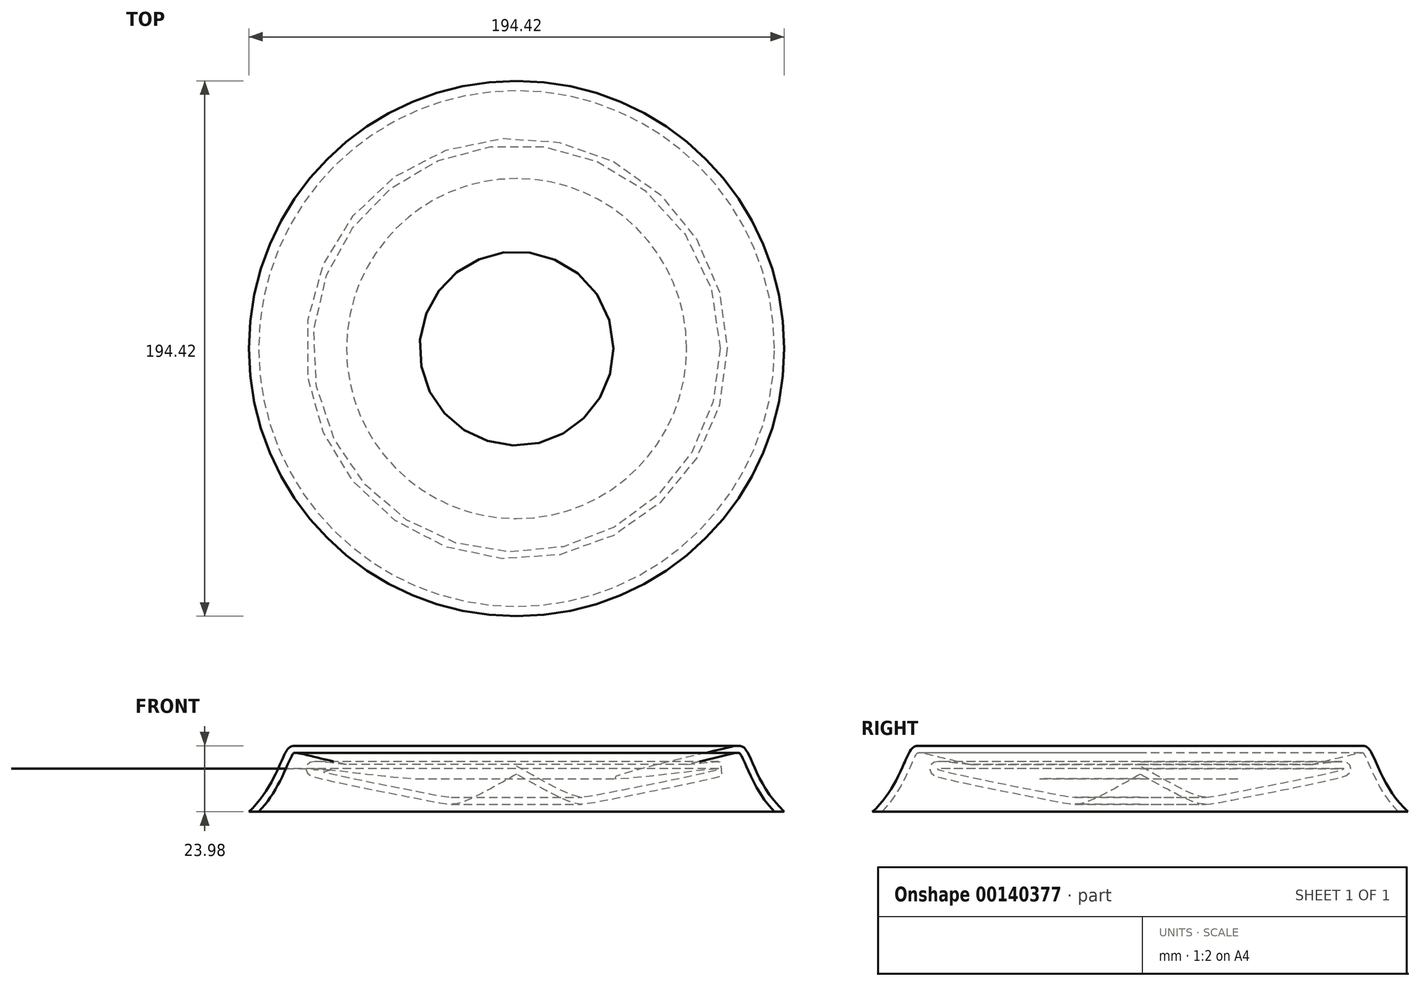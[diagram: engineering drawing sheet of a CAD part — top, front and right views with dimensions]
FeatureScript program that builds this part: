
annotation { "Feature Type Name" : "Feature", "Feature Type Description" : "" }
export const myFeature = defineFeature(function(context is Context, id is Id, definition is map)
    precondition{}
    {
        {
            var Q0;
            Q0=qCreatedBy(makeId("Front.planeOp"),FACE);
            var sketch = newSketch(context, id + "F0", { "sketchPlane" : qUnion([Q0])});
            skFitSpline(sketch, "E0", {"points": [v(97.2, 0) * mm, v(83.07, 22.76) * mm, v(74.23, 22.76) * mm, v(35.35, 12.15) * mm, v(73.79, 15.69) * mm, v(30.93, 6.4) * mm, v(20.33, 5.96) * mm, v(0, 16.57) * mm], "startDerivative": vector(-194.15, 182.07) * mm, "endDerivative": vector(-179.86, 102.06) * mm});
            skLineSegment(sketch, "E1", {"start": v(0, 16.57) * mm, "end": v(0, 0) * mm});
            skLineSegment(sketch, "E2", {"start": v(0, 0) * mm, "end": v(97.2, 0) * mm});
            skSolve(sketch);
        }
        {
            var Q0;
            Q0=makeQuery(id+"F0.imprint","IMPRINT",FACE,{"disambiguationData":[TD([[makeQuery(id+"F0.imprint","IMPRINT",EDGE,{"derivedFrom":sQuery(id+"F0.wireOp",EDGE,"E0")}),1.0]])]});
            var Q1;
            Q1=sQuery(id+"F0.wireOp",EDGE,"E1");
            revolve(context, id + "F1", {"entities" : qUnion([Q0]), "axis" : qUnion([Q1]), "revolveType" : RevolveType.FULL});
        }
        {
            var Q0;
            Q0=makeQuery(id+"F1.opRevolve","SWEPT_FACE",FACE,{"disambiguationData":[OSD([sQuery(id+"F0.wireOp",EDGE,"E2")])]});
            shell(context, id + "F2", {"entities" : qUnion([Q0]), "thickness" : 2.54 * mm});
        }
    });
